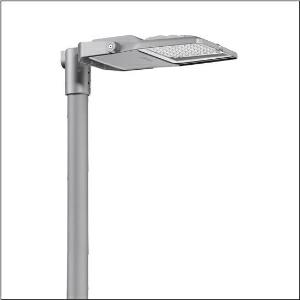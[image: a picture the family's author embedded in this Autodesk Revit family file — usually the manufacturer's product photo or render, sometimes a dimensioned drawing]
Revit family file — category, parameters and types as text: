
# Revit family: floodlight_fl_21_iq_mini___pl33t_5xa7772d4f3a_7ca2
name_source: partatom
category: Lighting Fixtures
units: mm (PartAtom-declared; Revit-internal decimal feet)

## family parameters
Cut with Voids When Loaded = No
Host = Face
Light Source = No
Part Type = Normal
Room Calculation Point = No
Round Connector Dimension = Use Diameter
Shared = No

## types (1)
- --- (1 x LED, 18390 lm, 143 W, 4000K)
    Apparent Load = 143 VA
    CIE Flux Codes = 26 75 99 100 100
    Color Rendering = 70
    Color Temperature = 4000K
    Default Elevation = 1800 mm
    Description = Floodlight FL 21 iQ mini, floodlight, primary light control with lens, of PMMA, primary optical cover: protective disc, of toughened safety glass, transparent, light distribution: PL33T, light emission: direct distribution, installation type: surface-mounted, LED, High Power LED, rated luminous flux: 18.390lm, luminous efficacy: 129lm/W, light colour: 740, colour temperature: 4000K, control: Auto-Match, Temp-Guard, Night-Set, Smart-Wire, Desk-Remote (wireless, voltage-free reading and setting of iQ features in the workshop via application-optimized NFC function/RFID function), optimised constant luminous flux control (CLO 2.0), Light-Fading, Lumen-Switch, with terminal, 6-pole, mains connection: 220..240V, AC, 50/60Hz, start of lifetime: 143W, end of service life: 152W, reduction: 61W, luminaire housing, of diecast aluminium, powder-coated, Siteco® metallic grey (DB 702S), corrosivity category C5 mid according to DIN EN ISO 12944, sealing non-destructively replaceable, please order mast flange separately, mast bracket, of steel, galvanised, powder-coated, protection rating (complete): IP66, insulation class (complete): insulation class II (safety insulation), certification: CE, ENEC, VDE, protection symbol: D, impact resistance: IK08, permissible operating ambient temperature: -40..+40°C, permissible operating ambient temperature for outdoor applications: -40..+50°C, standard: DIN EN 12944, LABS conformity tested according to VDMA 24364:2018-05, packaging unit: 1 piece

Light Distribution: PL33T
    Height = 70 mm
    Lamp = 1 x LED
    Lamp Light Flux = 18390 lm
    Lamp Power = 143 W
    Lamp count = 1
    Length = 485 mm
    Luminous efficacy = 129 lm/W
    Manufacturer = Siteco
    ModVariant = No
    Model = 5XA7772D4F3A
    Number of Poles = 1
    OnlyDefault = Yes
    Power Factor = 1
    Product Name = Floodlight FL 21 iQ mini | PL33T
    Product group = floodlight | pylon annexe
    ProductGroupID = 6200
    Protection Class = Protection class II
    Protection Degree = IP 66
    RLX_Detail_Level = 1
    RLX_Emergency_Light_Flux = 0 lm
    RLX_Emergency_Type = 0
    RLX_Emergency_Type_DB = No
    RlxData = <blob elided: 101513 chars, md5=91c6da28>
    Socket = socket
    Standby Power = 0 W
    System Light Flux = 18390 lm
    System Power = 143 W
    Type Comments = factory setting: luminous flux: 100 % | dim-lin: 254 | 730 mA
    Type Image = l_1007125.jpg
    URL = http://relux.com
    VarID = @adj_119113
    Voltage = 0 V
    Weight = 0.00 kg
    Width = 337 mm

## geometry (parser evidence)
native form markers: Blend x4, Sweep x13
no freeform markers — native parametric forms only
